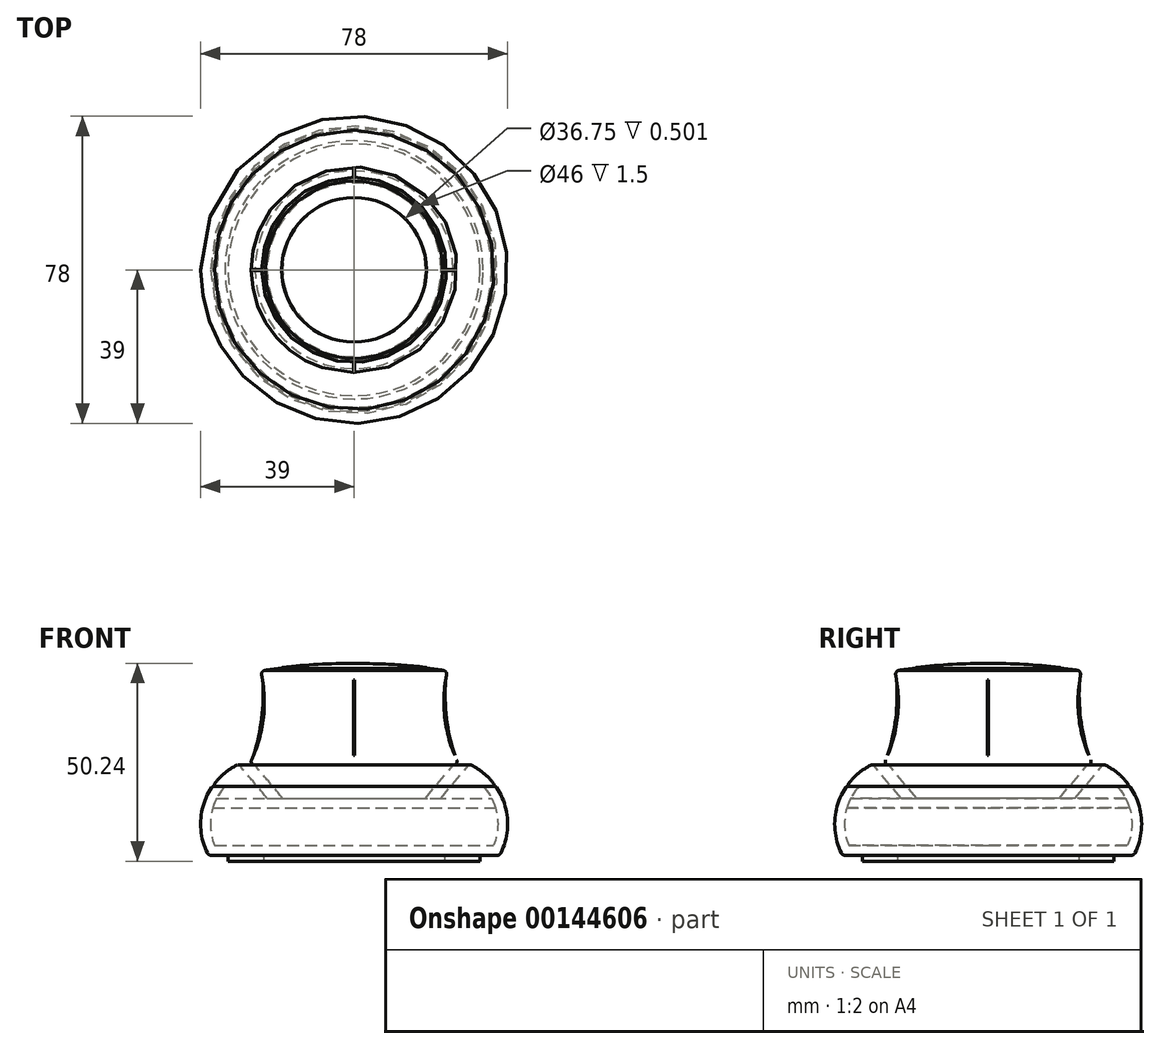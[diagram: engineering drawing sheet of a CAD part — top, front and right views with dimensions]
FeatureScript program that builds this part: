
annotation { "Feature Type Name" : "Feature", "Feature Type Description" : "" }
export const myFeature = defineFeature(function(context is Context, id is Id, definition is map)
    precondition{}
    {
        {
            var Q0;
            Q0=qCreatedBy(makeId("Front.planeOp"),FACE);
            var sketch = newSketch(context, id + "F0", { "sketchPlane" : qUnion([Q0])});
            skLineSegment(sketch, "E0", {"start": v(36.39, 0) * mm, "end": v(0, 0) * mm});
            skLineSegment(sketch, "E1", {"start": v(0, 0) * mm, "end": v(0, 17.5) * mm, "construction": true});
            skLineSegment(sketch, "E2", {"start": v(32.81, 17.5) * mm, "end": v(35.74, 17.5) * mm});
            skArc(sketch, "E3", {"start": v(35.4, 18.3) * mm, "mid": v(32.8, 20.95) * mm, "end": v(29.67, 22.95) * mm});
            skArc(sketch, "E4.0", {"start": v(35.42, 2.5) * mm, "mid": v(36.29, 10.38) * mm, "end": v(32.81, 17.5) * mm});
            skLineSegment(sketch, "E4.1", {"start": v(35.42, 2.5) * mm, "end": v(0, 2.5) * mm});
            skPoint(sketch, "E5.visualSharp", {"position": v(37, 0) * mm});
            skArc(sketch, "E5.filletArc", {"start": v(36.39, 0) * mm, "mid": v(36.92, 0.15) * mm, "end": v(37.29, 0.56) * mm});
            skPoint(sketch, "E6.newPointA", {"position": v(36, 17.5) * mm});
            skLineSegment(sketch, "E7", {"start": v(0, 0) * mm, "end": v(0, 2.5) * mm});
            skLineSegment(sketch, "E8", {"start": v(23, 0) * mm, "end": v(23, -1.5) * mm});
            skLineSegment(sketch, "E9", {"start": v(23, -1.5) * mm, "end": v(32, -1.5) * mm});
            skLineSegment(sketch, "E10", {"start": v(32, -1.5) * mm, "end": v(32, 0) * mm});
            skLineSegment(sketch, "E11", {"start": v(29.07, 22.82) * mm, "end": v(22.09, 14.5) * mm});
            skLineSegment(sketch, "E12", {"start": v(0, 14.5) * mm, "end": v(34.9, 14.5) * mm});
            skLineSegment(sketch, "E13", {"start": v(0, 14.5) * mm, "end": v(0, 12) * mm});
            skLineSegment(sketch, "E14", {"start": v(0, 12) * mm, "end": v(35.9, 12) * mm});
            skArc(sketch, "E15.filletArc", {"start": v(35, 17.5) * mm, "mid": v(35.46, 17.78) * mm, "end": v(35.4, 18.3) * mm});
            skArc(sketch, "E16", {"start": v(37.29, 0.56) * mm, "mid": v(38.96, 9.07) * mm, "end": v(36.15, 17.28) * mm});
            skArc(sketch, "E17.filletArc", {"start": v(36.15, 17.28) * mm, "mid": v(35.97, 17.44) * mm, "end": v(35.74, 17.5) * mm});
            skPoint(sketch, "E18.visualSharp", {"position": v(29.32, 23.12) * mm});
            skArc(sketch, "E18.filletArc", {"start": v(29.67, 22.95) * mm, "mid": v(29.35, 22.99) * mm, "end": v(29.07, 22.82) * mm});
            skLineSegment(sketch, "E19", {"start": v(0, 22.99) * mm, "end": v(25.13, 22.83) * mm});
            skPoint(sketch, "E19.startSnap0", {"position": v(29.35, 22.99) * mm});
            skLineSegment(sketch, "E20", {"start": v(0, 14.5) * mm, "end": v(0, 46.99) * mm});
            skLineSegment(sketch, "E21", {"start": v(0, 46.99) * mm, "end": v(18.38, 46.99) * mm});
            skArc(sketch, "E22", {"start": v(23.49, 45.8) * mm, "mid": v(23.06, 34.82) * mm, "end": v(26.05, 24.25) * mm});
            skPoint(sketch, "E23.visualSharp", {"position": v(23.75, 46.99) * mm});
            skArc(sketch, "E23.filletArc", {"start": v(23.49, 45.8) * mm, "mid": v(23.28, 46.62) * mm, "end": v(22.5, 46.99) * mm});
            skPoint(sketch, "E24.visualSharp", {"position": v(26.75, 22.82) * mm});
            skArc(sketch, "E24.filletArc", {"start": v(25.13, 22.83) * mm, "mid": v(25.98, 23.3) * mm, "end": v(26.05, 24.25) * mm});
            skLineSegment(sketch, "E25", {"start": v(25.13, 22.83) * mm, "end": v(18.14, 14.5) * mm});
            skArc(sketch, "E26", {"start": v(23.26, 44.49) * mm, "mid": v(23.48, 34.8) * mm, "end": v(25.57, 25.32) * mm});
            skArc(sketch, "E27", {"start": v(22.5, 46.99) * mm, "mid": v(20.44, 47.25) * mm, "end": v(18.38, 47.5) * mm});
            skLineSegment(sketch, "E28", {"start": v(18.38, 46.99) * mm, "end": v(18.38, 47.5) * mm});
            skArc(sketch, "E29.0", {"start": v(18.2, 47.76) * mm, "mid": v(9.12, 48.5) * mm, "end": v(0, 48.74) * mm});
            skPoint(sketch, "E30.orphan", {"position": v(0, 48.49) * mm});
            skLineSegment(sketch, "E31", {"start": v(18.38, 47.5) * mm, "end": v(18.38, 47.57) * mm});
            skLineSegment(sketch, "E32", {"start": v(0, 46.99) * mm, "end": v(0, 48.74) * mm});
            skPoint(sketch, "E33.visualSharp", {"position": v(18.38, 47.74) * mm});
            skArc(sketch, "E33.filletArc", {"start": v(18.38, 47.57) * mm, "mid": v(18.33, 47.7) * mm, "end": v(18.2, 47.76) * mm});
            skSolve(sketch);
        }
        {
            var Q0;
            Q0=makeQuery(id+"F0.imprint","IMPRINT",FACE,{"disambiguationData":[TD([[makeQuery(id+"F0.imprint","IMPRINT",EDGE,{"derivedFrom":sQuery(id+"F0.wireOp",EDGE,"E2")}),-1.0]])]});
            var Q1;
            Q1=sQuery(id+"F0.wireOp",EDGE,"E1");
            revolve(context, id + "F1", {"entities" : qUnion([Q0]), "axis" : qUnion([Q1]), "revolveType" : RevolveType.FULL});
        }
        {
            var Q0;
            {var subQ0=sQuery(id+"F0.wireOp",EDGE,"E8");Q0=makeQuery(id+"F0.imprint","IMPRINT",FACE,{"disambiguationData":[TD([[makeQuery(id+"F0.imprint","IMPRINT",EDGE,{"derivedFrom":subQ0}),1.0]])]});}
            var Q1;
            Q1=sQuery(id+"F0.wireOp",EDGE,"E1");
            revolve(context, id + "F2", {"entities" : qUnion([Q0]), "axis" : qUnion([Q1]), "revolveType" : RevolveType.FULL});
        }
        {
            var Q0;
            Q0=makeQuery(id+"F0.imprint","IMPRINT",FACE,{"disambiguationData":[TD([[makeQuery(id+"F0.imprint","IMPRINT",EDGE,{"derivedFrom":sQuery(id+"F0.wireOp",EDGE,"E3")}),1.0]])]});
            var Q1;
            Q1=makeQuery(id+"F0.imprint","IMPRINT",FACE,{"disambiguationData":[TD([[makeQuery(id+"F0.imprint","IMPRINT",EDGE,{"derivedFrom":sQuery(id+"F0.wireOp",EDGE,"E21")}),1.0]])]});
            var Q2;
            Q2=sQuery(id+"F0.wireOp",EDGE,"E1");
            revolve(context, id + "F3", {"entities" : qUnion([Q0, Q1]), "axis" : qUnion([Q2]), "revolveType" : RevolveType.FULL});
        }
        {
            var Q0;
            {var subQ0=sQuery(id+"F0.wireOp",EDGE,"E13");Q0=makeQuery(id+"F0.imprint","IMPRINT",FACE,{"disambiguationData":[TD([[makeQuery(id+"F0.imprint","IMPRINT",EDGE,{"derivedFrom":subQ0}),1.0]])]});}
            var Q1;
            Q1=sQuery(id+"F0.wireOp",EDGE,"E1");
            revolve(context, id + "F4", {"entities" : qUnion([Q0]), "axis" : qUnion([Q1]), "revolveType" : RevolveType.FULL});
        }
        {
            var Q0;
            {var subQ2=sQuery(id+"F0.wireOp",EDGE,"E19");Q0=makeQuery(id+"F0.imprint","IMPRINT",FACE,{"disambiguationData":[TD([[makeQuery(id+"F0.imprint","IMPRINT",EDGE,{"derivedFrom":subQ2}),1.0]])]});}
            var Q1;
            {var subQ4=sQuery(id+"F0.wireOp",EDGE,"E19");Q1=makeQuery(id+"F0.imprint","IMPRINT",FACE,{"disambiguationData":[TD([[makeQuery(id+"F0.imprint","IMPRINT",EDGE,{"derivedFrom":subQ4}),-1.0]])]});}
            var Q2;
            Q2=sQuery(id+"F0.wireOp",EDGE,"E20");
            revolve(context, id + "F5", {"entities" : qUnion([Q0, Q1]), "axis" : qUnion([Q2]), "revolveType" : RevolveType.FULL});
        }
        {
            var Q0;
            {var subQ0=sQuery(id+"F0.wireOp",EDGE,"E26");Q0=makeQuery(id+"F0.imprint","IMPRINT",FACE,{"disambiguationData":[TD([[makeQuery(id+"F0.imprint","IMPRINT",EDGE,{"derivedFrom":subQ0}),-1.0]])]});}
            extrude(context, id + "F6", {"entities" : qUnion([Q0]), "endBound" : BoundingType.SYMMETRIC, "depth" : .25 * mm});
        }
        {
            var Q0;
            Q0=makeQuery(id+"F6.opExtrude","SWEPT_BODY",BODY,{"disambiguationData":[OSD([sQuery(id+"F0.wireOp",EDGE,"E22"),sQuery(id+"F0.wireOp",EDGE,"E26")])]});
            var Q1;
            Q1=sQuery(id+"F0.wireOp",EDGE,"E20");
            circularPattern(context, id + "F7", {"operationType" : NewBodyOperationType.ADD, "entities" : qUnion([Q0]), "axis" : qUnion([Q1]), "angle" : 90 * degree, "instanceCount" : 4});
        }
    });
